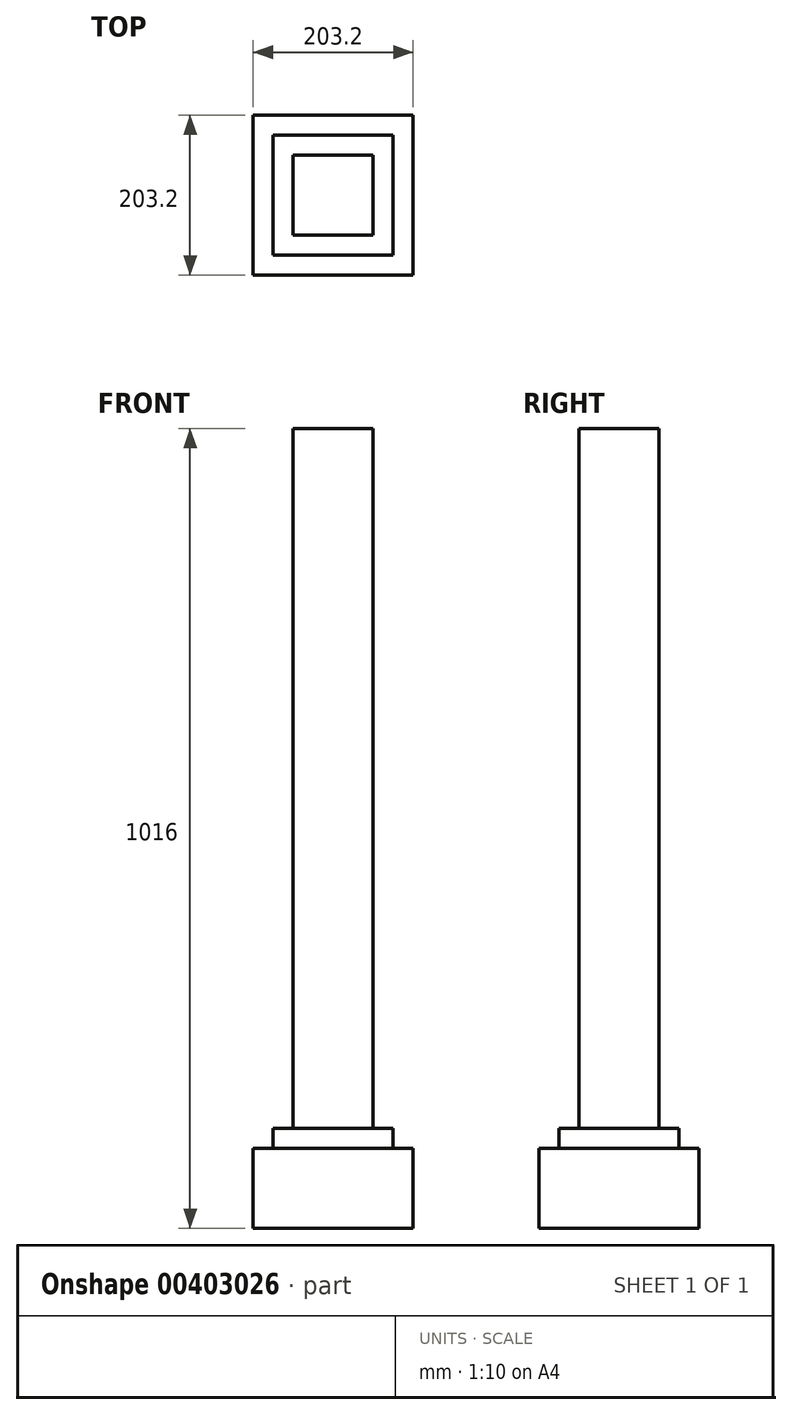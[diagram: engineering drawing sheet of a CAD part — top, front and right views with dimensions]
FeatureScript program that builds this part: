
annotation { "Feature Type Name" : "Feature", "Feature Type Description" : "" }
export const myFeature = defineFeature(function(context is Context, id is Id, definition is map)
    precondition{}
    {
        {
            var Q0;
            Q0=qCreatedBy(makeId("Top.planeOp"),FACE);
            var sketch = newSketch(context, id + "F0", { "sketchPlane" : qUnion([Q0])});
            skLineSegment(sketch, "E0.bottom", {"start": v(0, 0) * mm, "end": v(101.6, 0) * mm});
            skLineSegment(sketch, "E0.top", {"start": v(0, -101.6) * mm, "end": v(101.6, -101.6) * mm});
            skLineSegment(sketch, "E0.left", {"start": v(0, 0) * mm, "end": v(0, -101.6) * mm});
            skLineSegment(sketch, "E0.right", {"start": v(101.6, 0) * mm, "end": v(101.6, -101.6) * mm});
            skSolve(sketch);
        }
        {
            var Q0;
            Q0=makeQuery(id+"F0.imprint","IMPRINT",FACE,{"disambiguationData":[TD([[makeQuery(id+"F0.imprint","IMPRINT",EDGE,{"derivedFrom":sQuery(id+"F0.wireOp",EDGE,"E0.bottom")}),-1.0]])]});
            extrude(context, id + "F1", {"entities" : qUnion([Q0]), "depth" : 1016 * mm});
        }
        {
            var Q0;
            Q0=makeQuery(id+"F1.opExtrude","SWEPT_FACE",FACE,{"disambiguationData":[OSD([sQuery(id+"F0.wireOp",EDGE,"E0.left")])]});
            var sketch = newSketch(context, id + "F2", { "sketchPlane" : qUnion([Q0])});
            skLineSegment(sketch, "E1", {"start": v(50.8, 1016) * mm, "end": v(50.8, 0) * mm});
            skSolve(sketch);
        }
        {
            var Q0;
            {var subQ0=sQuery(id+"F2.wireOp",EDGE,"E1");Q0=makeQuery(id+"F2.imprint","IMPRINT",FACE,{"disambiguationData":[TD([[makeQuery(id+"F2.imprint","IMPRINT",EDGE,{"derivedFrom":subQ0}),-1.0]])]});}
            var sketch = newSketch(context, id + "F3", { "sketchPlane" : qUnion([Q0])});
            skLineSegment(sketch, "E2", {"start": v(50.8, 865.14) * mm, "end": v(23.86, 838.2) * mm});
            skLineSegment(sketch, "E3", {"start": v(23.86, 838.2) * mm, "end": v(50.8, 811.26) * mm});
            skLineSegment(sketch, "E4", {"start": v(50.8, 811.26) * mm, "end": v(77.74, 838.2) * mm});
            skLineSegment(sketch, "E5", {"start": v(77.74, 838.2) * mm, "end": v(50.8, 865.14) * mm});
            skSolve(sketch);
        }
        {
            var Q0;
            Q0=qCreatedBy(makeId("Top.planeOp"),FACE);
            var sketch = newSketch(context, id + "F4", { "sketchPlane" : qUnion([Q0])});
            skLineSegment(sketch, "E6.bottom", {"start": v(-25.4, 25.4) * mm, "end": v(127, 25.4) * mm});
            skLineSegment(sketch, "E6.top", {"start": v(-25.4, -127) * mm, "end": v(127, -127) * mm});
            skLineSegment(sketch, "E6.left", {"start": v(-25.4, 25.4) * mm, "end": v(-25.4, -127) * mm});
            skLineSegment(sketch, "E6.right", {"start": v(127, 25.4) * mm, "end": v(127, -127) * mm});
            skSolve(sketch);
        }
        {
            var Q0;
            Q0=makeQuery(id+"F4.imprint","IMPRINT",FACE,{"disambiguationData":[TD([[makeQuery(id+"F4.imprint","IMPRINT",EDGE,{"derivedFrom":sQuery(id+"F4.wireOp",EDGE,"E6.bottom")}),-1.0]])]});
            extrude(context, id + "F5", {"entities" : qUnion([Q0]), "operationType" : NewBodyOperationType.ADD, "depth" : 127 * mm});
        }
        {
            var Q0;
            Q0=qCreatedBy(makeId("Top.planeOp"),FACE);
            var sketch = newSketch(context, id + "F6", { "sketchPlane" : qUnion([Q0])});
            skLineSegment(sketch, "E7.bottom", {"start": v(-50.8, 50.8) * mm, "end": v(152.4, 50.8) * mm});
            skLineSegment(sketch, "E7.top", {"start": v(-50.8, -152.4) * mm, "end": v(152.4, -152.4) * mm});
            skLineSegment(sketch, "E7.left", {"start": v(-50.8, 50.8) * mm, "end": v(-50.8, -152.4) * mm});
            skLineSegment(sketch, "E7.right", {"start": v(152.4, 50.8) * mm, "end": v(152.4, -152.4) * mm});
            skSolve(sketch);
        }
        {
            var Q0;
            Q0=makeQuery(id+"F6.imprint","IMPRINT",FACE,{"disambiguationData":[TD([[makeQuery(id+"F6.imprint","IMPRINT",EDGE,{"derivedFrom":sQuery(id+"F6.wireOp",EDGE,"E7.bottom")}),-1.0]])]});
            extrude(context, id + "F7", {"entities" : qUnion([Q0]), "operationType" : NewBodyOperationType.ADD, "depth" : 101.6 * mm});
        }
    });
